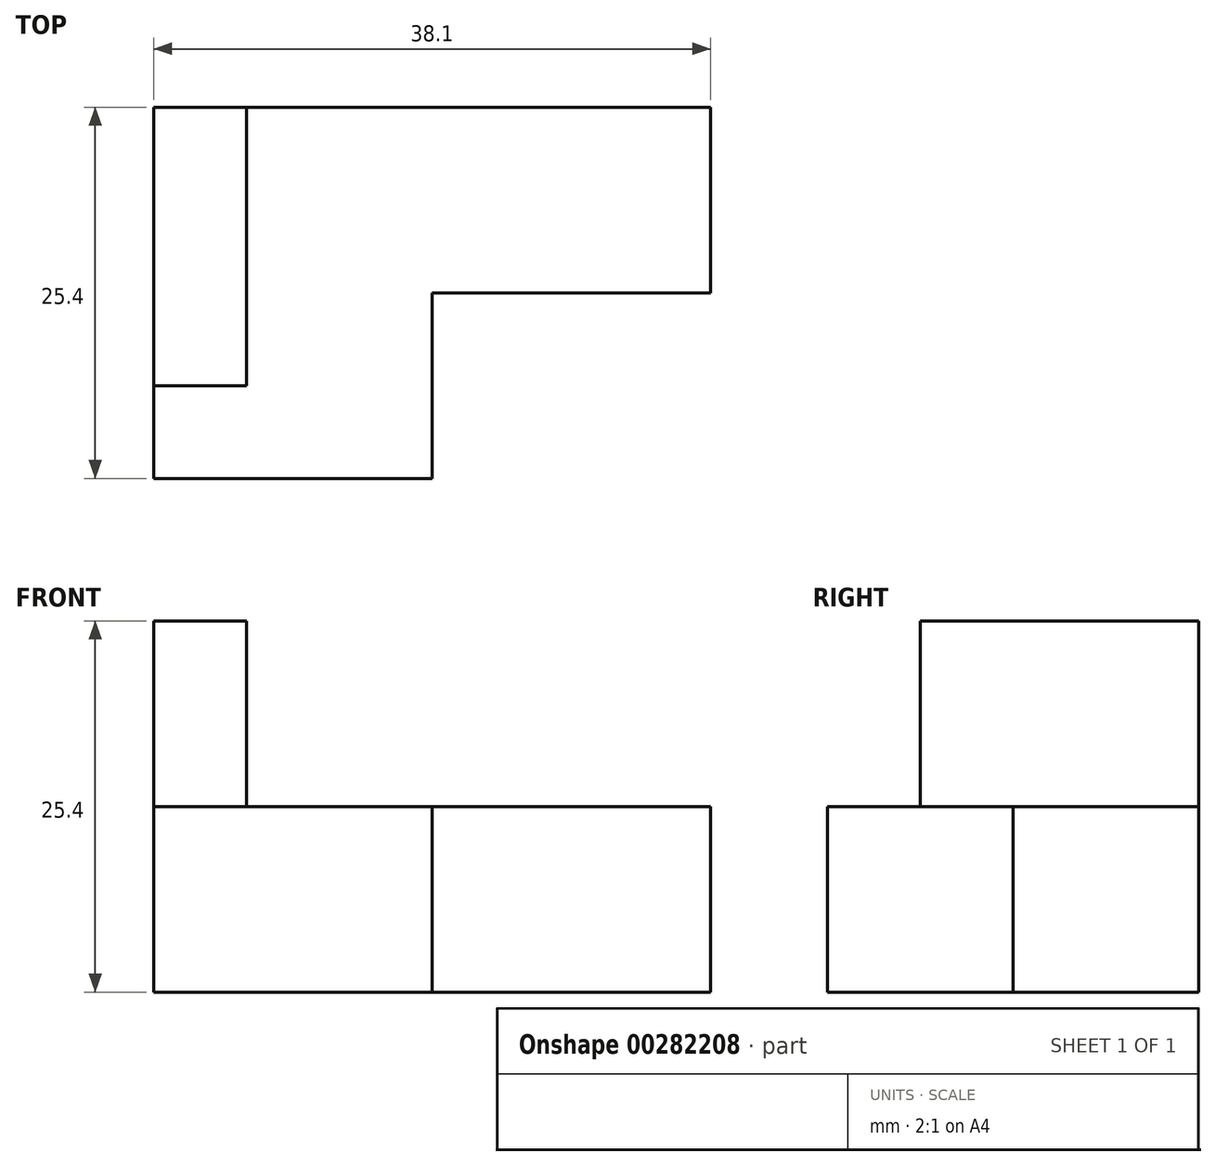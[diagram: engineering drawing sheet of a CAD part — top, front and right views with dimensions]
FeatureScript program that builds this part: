
annotation { "Feature Type Name" : "Feature", "Feature Type Description" : "" }
export const myFeature = defineFeature(function(context is Context, id is Id, definition is map)
    precondition{}
    {
        {
            var Q0;
            Q0=qCreatedBy(makeId("Top.planeOp"),FACE);
            var sketch = newSketch(context, id + "F0", { "sketchPlane" : qUnion([Q0])});
            skLineSegment(sketch, "E0", {"start": v(0, 0) * mm, "end": v(0, -25.4) * mm});
            skLineSegment(sketch, "E1", {"start": v(0, -25.4) * mm, "end": v(19.05, -25.4) * mm});
            skLineSegment(sketch, "E2", {"start": v(19.05, -25.4) * mm, "end": v(19.05, -12.7) * mm});
            skLineSegment(sketch, "E3", {"start": v(19.05, -12.7) * mm, "end": v(38.1, -12.7) * mm});
            skLineSegment(sketch, "E4", {"start": v(38.1, -12.7) * mm, "end": v(38.1, 0) * mm});
            skLineSegment(sketch, "E5", {"start": v(38.1, 0) * mm, "end": v(0, 0) * mm});
            skSolve(sketch);
        }
        {
            var Q0;
            Q0=makeQuery(id+"F0.imprint","IMPRINT",FACE,{"disambiguationData":[TD([[makeQuery(id+"F0.imprint","IMPRINT",EDGE,{"derivedFrom":sQuery(id+"F0.wireOp",EDGE,"E0")}),1.0]])]});
            extrude(context, id + "F1", {"entities" : qUnion([Q0]), "depth" : 12.7 * mm});
        }
        {
            var Q0;
            Q0=qCreatedBy(makeId("Right.planeOp"),FACE);
            var sketch = newSketch(context, id + "F2", { "sketchPlane" : qUnion([Q0])});
            skLineSegment(sketch, "E6", {"start": v(0, 12.7) * mm, "end": v(0, 25.4) * mm});
            skLineSegment(sketch, "E7", {"start": v(0, 25.4) * mm, "end": v(-19.05, 25.4) * mm});
            skLineSegment(sketch, "E8", {"start": v(-19.05, 25.4) * mm, "end": v(-19.05, 12.7) * mm});
            skLineSegment(sketch, "E9", {"start": v(-19.05, 12.7) * mm, "end": v(0, 12.7) * mm});
            skSolve(sketch);
        }
        {
            var Q0;
            Q0=makeQuery(id+"F2.imprint","IMPRINT",FACE,{"disambiguationData":[TD([[makeQuery(id+"F2.imprint","IMPRINT",EDGE,{"derivedFrom":sQuery(id+"F2.wireOp",EDGE,"E6")}),1.0]])]});
            extrude(context, id + "F3", {"entities" : qUnion([Q0]), "operationType" : NewBodyOperationType.ADD, "depth" : 6.35 * mm});
        }
    });
